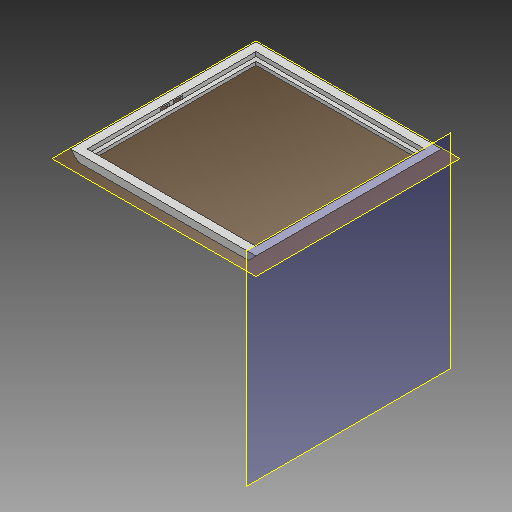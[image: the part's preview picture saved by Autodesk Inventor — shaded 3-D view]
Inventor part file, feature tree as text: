
AUTODESK INVENTOR PART (.ipt)
format: ipt  version: 2018.3 (Build 223284000, 284)  size: 205,824 bytes
history: native  units: mm
features: reference x20, other x12, extrude x6, sketch x6, plane x2, chamfer x1, projected_geometry x1
ambient origin geometry x8: Origin, YZ Plane, XZ Plane, XY Plane, X Axis, Y Axis, Z Axis, Center Point
bodies: Volumenkörper1 (feature_tree)
feature tree (48):
  extrude  "Extrusion1"  [1 undecoded]
  plane  "Arbeitsebene1"
  extrude  "Extrusion2"  Depth=10.0mm
  extrude  "Extrusion3"  Depth=10.0mm
  plane  "Arbeitsebene3"
  extrude  "Extrusion4"  Depth=8.0mm TaperAngle=0.0deg
  extrude  "Extrusion5"  Depth=2.0mm TaperAngle=0.0deg
  extrude  "Extrusion6"  Depth=18.0mm TaperAngle=45.0deg
  chamfer  "Fase2"  [1 undecoded]
  sketch  "Skizze1"  dims[d0=18.0mm d1=0.0mm d5=-20.0mm]
  reference  "Referenz1"
  reference  "Referenz2"
  reference  "Referenz3"
  reference  "Referenz4"
  reference  "Referenz5"
  sketch  "Skizze3"  dims[d6=17.0mm d7=0.0mm d8=10.0mm]
  reference  "Referenz12"
  reference  "Referenz13"
  reference  "Referenz14"
  reference  "Referenz15"
  reference  "Referenz16"
  reference  "Referenz17"
  reference  "Referenz18"
  reference  "Referenz19"
  sketch  "Skizze5"  dims[d9=10.0mm d10=10.0mm]
  sketch  "Skizze6"  dims[d11=10.0mm d12=8.0mm d13=0.0mm]
  reference  "Referenz20"
  reference  "Referenz21"
  reference  "Referenz22"
  reference  "Referenz23"
  reference  "Referenz24"
  reference  "Referenz25"
  sketch  "Skizze7"  dims[d14=25.0mm d15=0.0mm d16=2.0mm d17=0.0mm]
  projected_geometry  "Projizierte Kontur1"
  sketch  "Skizze8"  dims[d18=2.0mm d19=0.0mm d20=18.0mm d21=2.0mm d22=45.0deg]
  reference  "Referenz26"
  parser-record x2  (decoder bookkeeping rows leaked as tree rows — omitted from the tree; the rows remain in map.json)
  other  "SmartCube_Quadratisch.iam"
  other  "Wand2_MIR:1"
  other  "Wand1:1"
  other  "Wand1_MIR:1"
  other  "Wand2:1"
  other  "PV_Modul:1"
  other  "<userpath>\Documents\Dipl\Smartcube_Construction\Version_3\Baugruppe1.iam"
  other  "Baugruppe1.iam"
  other  "PV_Ramen_CPY_3_2:1"
  other  "PV_Modul_CPY_3:1"
note: 2 required parameter values undecoded (feature->parameter linkage not recoverable at this tier; creation-order binding heuristic only, values carry confidence <= 0.55)
note: 2 file-system paths scrubbed to <path> (originals preserved in map.json)
